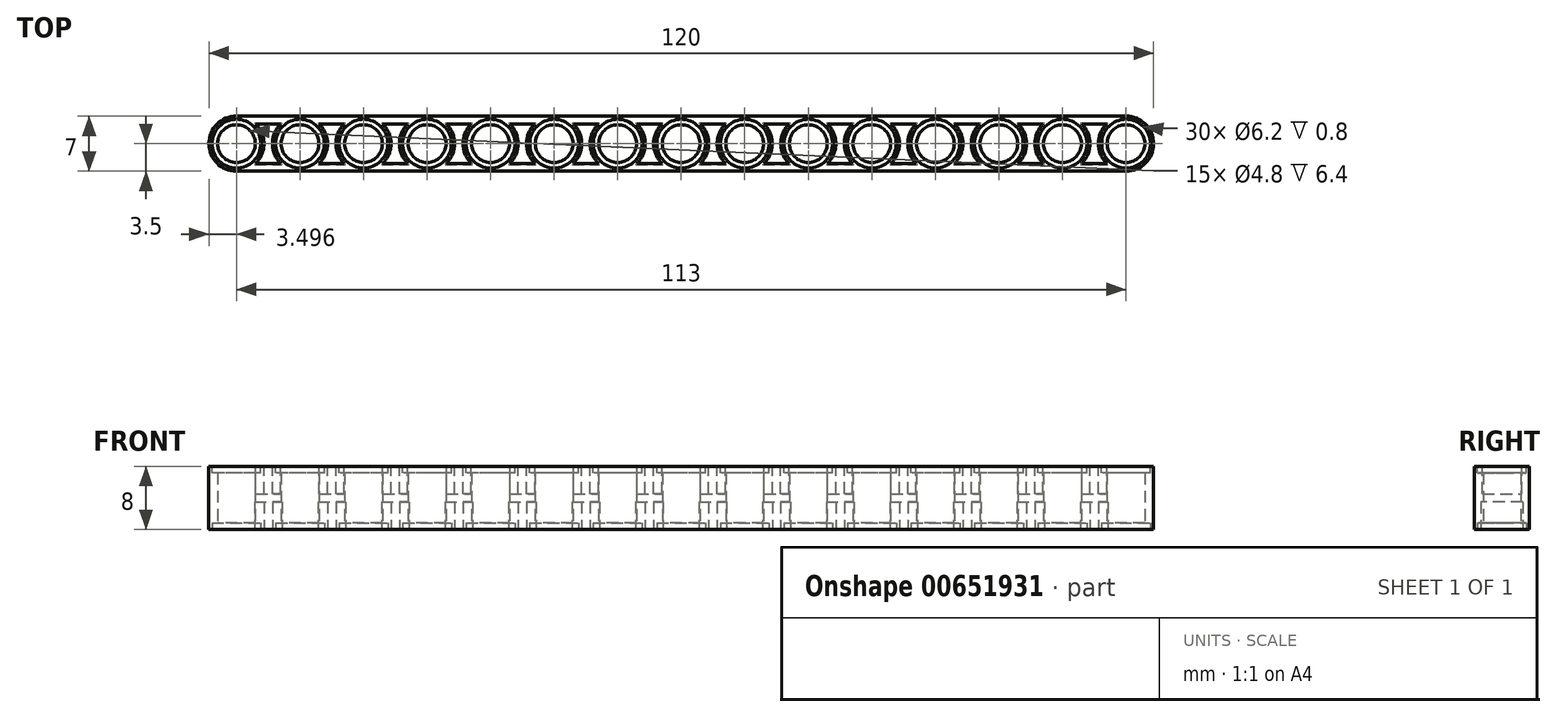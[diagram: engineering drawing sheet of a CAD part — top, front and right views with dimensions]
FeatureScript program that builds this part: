
annotation { "Feature Type Name" : "Feature", "Feature Type Description" : "" }
export const myFeature = defineFeature(function(context is Context, id is Id, definition is map)
    precondition{}
    {
        {
            var Q0;
            Q0=qCreatedBy(makeId("Top.planeOp"),FACE);
            var sketch = newSketch(context, id + "F0", { "sketchPlane" : qUnion([Q0])});
            skLineSegment(sketch, "E0.bottom", {"start": v(-24.08, -14.52) * mm, "end": v(88.92, -14.52) * mm});
            skLineSegment(sketch, "E0.top", {"start": v(-24.08, -21.52) * mm, "end": v(88.92, -21.52) * mm});
            skLineSegment(sketch, "E0.left", {"start": v(-27.58, -18.02) * mm, "end": v(-27.58, -18.02) * mm});
            skLineSegment(sketch, "E0.right", {"start": v(92.42, -18.02) * mm, "end": v(92.42, -18.02) * mm});
            skPoint(sketch, "E1.visualSharp", {"position": v(-27.58, -14.52) * mm});
            skArc(sketch, "E1.filletArc", {"start": v(-24.08, -14.52) * mm, "mid": v(-26.56, -15.55) * mm, "end": v(-27.58, -18.02) * mm});
            skPoint(sketch, "E2.visualSharp", {"position": v(-27.58, -21.52) * mm});
            skArc(sketch, "E2.filletArc", {"start": v(-27.58, -18.02) * mm, "mid": v(-26.56, -20.5) * mm, "end": v(-24.08, -21.52) * mm});
            skPoint(sketch, "E3.visualSharp", {"position": v(92.42, -21.52) * mm});
            skArc(sketch, "E3.filletArc", {"start": v(88.92, -21.52) * mm, "mid": v(91.4, -20.5) * mm, "end": v(92.42, -18.02) * mm});
            skPoint(sketch, "E4.visualSharp", {"position": v(92.42, -14.52) * mm});
            skArc(sketch, "E4.filletArc", {"start": v(92.42, -18.02) * mm, "mid": v(91.4, -15.55) * mm, "end": v(88.92, -14.52) * mm});
            skCircle(sketch, "E5", {"center": v(-24.08, -18.02) * mm, "radius": 2.4 * mm});
            skCircle(sketch, "E6.1.0.0", {"center": v(-16.01, -18.02) * mm, "radius": 2.4 * mm});
            skLineSegment(sketch, "E6.1.0.1", {"start": v(-16.01, -21.52) * mm, "end": v(96.99, -21.52) * mm});
            skCircle(sketch, "E6.2.0.0", {"center": v(-7.94, -18.02) * mm, "radius": 2.4 * mm});
            skLineSegment(sketch, "E6.2.0.1", {"start": v(-7.94, -21.52) * mm, "end": v(105.06, -21.52) * mm});
            skCircle(sketch, "E6.3.0.0", {"center": v(0.13, -18.02) * mm, "radius": 2.4 * mm});
            skLineSegment(sketch, "E6.3.0.1", {"start": v(0.13, -21.52) * mm, "end": v(113.13, -21.52) * mm});
            skCircle(sketch, "E6.4.0.0", {"center": v(8.2, -18.02) * mm, "radius": 2.4 * mm});
            skLineSegment(sketch, "E6.4.0.1", {"start": v(8.2, -21.52) * mm, "end": v(121.2, -21.52) * mm});
            skCircle(sketch, "E6.5.0.0", {"center": v(16.27, -18.02) * mm, "radius": 2.4 * mm});
            skLineSegment(sketch, "E6.5.0.1", {"start": v(16.27, -21.52) * mm, "end": v(129.27, -21.52) * mm});
            skCircle(sketch, "E6.6.0.0", {"center": v(24.34, -18.02) * mm, "radius": 2.4 * mm});
            skCircle(sketch, "E6.7.0.0", {"center": v(32.42, -18.02) * mm, "radius": 2.4 * mm});
            skLineSegment(sketch, "E6.7.0.1", {"start": v(32.42, -21.52) * mm, "end": v(145.42, -21.52) * mm});
            skCircle(sketch, "E6.8.0.0", {"center": v(40.49, -18.02) * mm, "radius": 2.4 * mm});
            skLineSegment(sketch, "E6.8.0.1", {"start": v(40.49, -21.52) * mm, "end": v(153.49, -21.52) * mm});
            skCircle(sketch, "E6.9.0.0", {"center": v(48.56, -18.02) * mm, "radius": 2.4 * mm});
            skLineSegment(sketch, "E6.9.0.1", {"start": v(48.56, -21.52) * mm, "end": v(161.56, -21.52) * mm});
            skCircle(sketch, "E6.10.0.0", {"center": v(56.63, -18.02) * mm, "radius": 2.4 * mm});
            skLineSegment(sketch, "E6.10.0.1", {"start": v(56.63, -21.52) * mm, "end": v(169.63, -21.52) * mm});
            skCircle(sketch, "E6.11.0.0", {"center": v(64.7, -18.02) * mm, "radius": 2.4 * mm});
            skLineSegment(sketch, "E6.11.0.1", {"start": v(64.7, -21.52) * mm, "end": v(177.7, -21.52) * mm});
            skCircle(sketch, "E6.12.0.0", {"center": v(72.77, -18.02) * mm, "radius": 2.4 * mm});
            skLineSegment(sketch, "E6.12.0.1", {"start": v(72.77, -21.52) * mm, "end": v(185.77, -21.52) * mm});
            skCircle(sketch, "E6.13.0.0", {"center": v(80.84, -18.02) * mm, "radius": 2.4 * mm});
            skLineSegment(sketch, "E6.13.0.1", {"start": v(80.84, -21.52) * mm, "end": v(193.84, -21.52) * mm});
            skCircle(sketch, "E6.14.0.0", {"center": v(88.92, -18.02) * mm, "radius": 2.4 * mm});
            skLineSegment(sketch, "E6.direction1", {"start": v(-24.08, -18.02) * mm, "end": v(-16.01, -18.02) * mm, "construction": true});
            skSolve(sketch);
        }
        {
            var Q0;
            Q0=makeQuery(id+"F0.imprint","IMPRINT",FACE,{"disambiguationData":[TD([[makeQuery(id+"F0.imprint","IMPRINT",EDGE,{"derivedFrom":sQuery(id+"F0.wireOp",EDGE,"E0.bottom")}),-1.0]])]});
            extrude(context, id + "F1", {"entities" : qUnion([Q0]), "depth" : 8 * mm, "offsetDistance" : 25 * mm});
        }
        {
            var Q0;
            Q0=makeQuery(id+"F1.opExtrude","CAP_FACE",FACE,{"disambiguationData":[OSD([sQuery(id+"F0.wireOp",EDGE,"E0.bottom"),sQuery(id+"F0.wireOp",EDGE,"E0.top"),sQuery(id+"F0.wireOp",EDGE,"E1.filletArc"),sQuery(id+"F0.wireOp",EDGE,"E2.filletArc"),sQuery(id+"F0.wireOp",EDGE,"E3.filletArc"),sQuery(id+"F0.wireOp",EDGE,"E4.filletArc"),sQuery(id+"F0.wireOp",EDGE,"E5"),sQuery(id+"F0.wireOp",EDGE,"E6.1.0.0"),sQuery(id+"F0.wireOp",EDGE,"E6.1.0.1"),sQuery(id+"F0.wireOp",EDGE,"E6.2.0.0"),sQuery(id+"F0.wireOp",EDGE,"E6.2.0.1"),sQuery(id+"F0.wireOp",EDGE,"E6.3.0.0"),sQuery(id+"F0.wireOp",EDGE,"E6.3.0.1"),sQuery(id+"F0.wireOp",EDGE,"E6.4.0.0"),sQuery(id+"F0.wireOp",EDGE,"E6.4.0.1"),sQuery(id+"F0.wireOp",EDGE,"E6.5.0.0"),sQuery(id+"F0.wireOp",EDGE,"E6.5.0.1"),sQuery(id+"F0.wireOp",EDGE,"E6.6.0.0"),sQuery(id+"F0.wireOp",EDGE,"E6.7.0.0"),sQuery(id+"F0.wireOp",EDGE,"E6.7.0.1"),sQuery(id+"F0.wireOp",EDGE,"E6.8.0.0"),sQuery(id+"F0.wireOp",EDGE,"E6.8.0.1"),sQuery(id+"F0.wireOp",EDGE,"E6.9.0.0"),sQuery(id+"F0.wireOp",EDGE,"E6.9.0.1"),sQuery(id+"F0.wireOp",EDGE,"E6.10.0.0"),sQuery(id+"F0.wireOp",EDGE,"E6.10.0.1"),sQuery(id+"F0.wireOp",EDGE,"E6.11.0.0"),sQuery(id+"F0.wireOp",EDGE,"E6.11.0.1"),sQuery(id+"F0.wireOp",EDGE,"E6.12.0.0"),sQuery(id+"F0.wireOp",EDGE,"E6.12.0.1"),sQuery(id+"F0.wireOp",EDGE,"E6.13.0.0"),sQuery(id+"F0.wireOp",EDGE,"E6.13.0.1"),sQuery(id+"F0.wireOp",EDGE,"E6.14.0.0")])],"isStart":false});
            var sketch = newSketch(context, id + "F2", { "sketchPlane" : qUnion([Q0])});
            skCircle(sketch, "E7", {"center": v(-24.08, -18.02) * mm, "radius": 3.1 * mm});
            skCircle(sketch, "E8.1.0.0", {"center": v(-16.01, -18.02) * mm, "radius": 3.1 * mm});
            skCircle(sketch, "E8.2.0.0", {"center": v(-7.94, -18.02) * mm, "radius": 3.1 * mm});
            skCircle(sketch, "E8.3.0.0", {"center": v(0.13, -18.02) * mm, "radius": 3.1 * mm});
            skCircle(sketch, "E8.4.0.0", {"center": v(8.2, -18.02) * mm, "radius": 3.1 * mm});
            skCircle(sketch, "E8.5.0.0", {"center": v(16.27, -18.02) * mm, "radius": 3.1 * mm});
            skCircle(sketch, "E8.6.0.0", {"center": v(24.34, -18.02) * mm, "radius": 3.1 * mm});
            skCircle(sketch, "E8.7.0.0", {"center": v(32.42, -18.02) * mm, "radius": 3.1 * mm});
            skCircle(sketch, "E8.8.0.0", {"center": v(40.49, -18.02) * mm, "radius": 3.1 * mm});
            skCircle(sketch, "E8.9.0.0", {"center": v(48.56, -18.02) * mm, "radius": 3.1 * mm});
            skCircle(sketch, "E8.10.0.0", {"center": v(56.63, -18.02) * mm, "radius": 3.1 * mm});
            skCircle(sketch, "E8.11.0.0", {"center": v(64.7, -18.02) * mm, "radius": 3.1 * mm});
            skCircle(sketch, "E8.12.0.0", {"center": v(72.77, -18.02) * mm, "radius": 3.1 * mm});
            skCircle(sketch, "E8.13.0.0", {"center": v(80.84, -18.02) * mm, "radius": 3.1 * mm});
            skCircle(sketch, "E8.14.0.0", {"center": v(88.92, -18.02) * mm, "radius": 3.1 * mm});
            skLineSegment(sketch, "E8.direction1", {"start": v(-24.08, -18.02) * mm, "end": v(-16.01, -18.02) * mm, "construction": true});
            skSolve(sketch);
        }
        {
            var Q0;
            Q0=makeQuery(id+"F2.imprint","IMPRINT",FACE,{"disambiguationData":[TD([[makeQuery(id+"F2.imprint","IMPRINT",EDGE,{"derivedFrom":sQuery(id+"F2.wireOp",EDGE,"E8.14.0.0")}),1.0]])]});
            var Q1;
            Q1=makeQuery(id+"F2.imprint","IMPRINT",FACE,{"disambiguationData":[TD([[makeQuery(id+"F2.imprint","IMPRINT",EDGE,{"derivedFrom":sQuery(id+"F2.wireOp",EDGE,"E8.13.0.0")}),1.0]])]});
            var Q2;
            Q2=makeQuery(id+"F2.imprint","IMPRINT",FACE,{"disambiguationData":[TD([[makeQuery(id+"F2.imprint","IMPRINT",EDGE,{"derivedFrom":sQuery(id+"F2.wireOp",EDGE,"E8.12.0.0")}),1.0]])]});
            var Q3;
            Q3=makeQuery(id+"F2.imprint","IMPRINT",FACE,{"disambiguationData":[TD([[makeQuery(id+"F2.imprint","IMPRINT",EDGE,{"derivedFrom":sQuery(id+"F2.wireOp",EDGE,"E8.11.0.0")}),1.0]])]});
            var Q4;
            Q4=makeQuery(id+"F2.imprint","IMPRINT",FACE,{"disambiguationData":[TD([[makeQuery(id+"F2.imprint","IMPRINT",EDGE,{"derivedFrom":sQuery(id+"F2.wireOp",EDGE,"E8.10.0.0")}),1.0]])]});
            var Q5;
            Q5=makeQuery(id+"F2.imprint","IMPRINT",FACE,{"disambiguationData":[TD([[makeQuery(id+"F2.imprint","IMPRINT",EDGE,{"derivedFrom":sQuery(id+"F2.wireOp",EDGE,"E8.9.0.0")}),1.0]])]});
            var Q6;
            Q6=makeQuery(id+"F2.imprint","IMPRINT",FACE,{"disambiguationData":[TD([[makeQuery(id+"F2.imprint","IMPRINT",EDGE,{"derivedFrom":sQuery(id+"F2.wireOp",EDGE,"E8.8.0.0")}),1.0]])]});
            var Q7;
            Q7=makeQuery(id+"F2.imprint","IMPRINT",FACE,{"disambiguationData":[TD([[makeQuery(id+"F2.imprint","IMPRINT",EDGE,{"derivedFrom":sQuery(id+"F2.wireOp",EDGE,"E8.7.0.0")}),1.0]])]});
            var Q8;
            Q8=makeQuery(id+"F2.imprint","IMPRINT",FACE,{"disambiguationData":[TD([[makeQuery(id+"F2.imprint","IMPRINT",EDGE,{"derivedFrom":sQuery(id+"F2.wireOp",EDGE,"E8.6.0.0")}),1.0]])]});
            var Q9;
            Q9=makeQuery(id+"F2.imprint","IMPRINT",FACE,{"disambiguationData":[TD([[makeQuery(id+"F2.imprint","IMPRINT",EDGE,{"derivedFrom":sQuery(id+"F2.wireOp",EDGE,"E8.5.0.0")}),1.0]])]});
            var Q10;
            Q10=makeQuery(id+"F2.imprint","IMPRINT",FACE,{"disambiguationData":[TD([[makeQuery(id+"F2.imprint","IMPRINT",EDGE,{"derivedFrom":sQuery(id+"F2.wireOp",EDGE,"E8.4.0.0")}),1.0]])]});
            var Q11;
            Q11=makeQuery(id+"F2.imprint","IMPRINT",FACE,{"disambiguationData":[TD([[makeQuery(id+"F2.imprint","IMPRINT",EDGE,{"derivedFrom":sQuery(id+"F2.wireOp",EDGE,"E8.3.0.0")}),1.0]])]});
            var Q12;
            Q12=makeQuery(id+"F2.imprint","IMPRINT",FACE,{"disambiguationData":[TD([[makeQuery(id+"F2.imprint","IMPRINT",EDGE,{"derivedFrom":sQuery(id+"F2.wireOp",EDGE,"E8.2.0.0")}),1.0]])]});
            var Q13;
            Q13=makeQuery(id+"F2.imprint","IMPRINT",FACE,{"disambiguationData":[TD([[makeQuery(id+"F2.imprint","IMPRINT",EDGE,{"derivedFrom":sQuery(id+"F2.wireOp",EDGE,"E8.1.0.0")}),1.0]])]});
            var Q14;
            Q14=makeQuery(id+"F2.imprint","IMPRINT",FACE,{"disambiguationData":[TD([[makeQuery(id+"F2.imprint","IMPRINT",EDGE,{"derivedFrom":sQuery(id+"F2.wireOp",EDGE,"E7")}),1.0]])]});
            extrude(context, id + "F3", {"entities" : qUnion([Q0, Q1, Q2, Q3, Q4, Q5, Q6, Q7, Q8, Q9, Q10, Q11, Q12, Q13, Q14]), "operationType" : NewBodyOperationType.REMOVE, "oppositeDirection" : true, "depth" : 0.8 * mm, "offsetDistance" : 25 * mm});
        }
        {
            var Q0;
            Q0=makeQuery(id+"F1.opExtrude","CAP_FACE",FACE,{"disambiguationData":[OSD([sQuery(id+"F0.wireOp",EDGE,"E0.bottom"),sQuery(id+"F0.wireOp",EDGE,"E0.top"),sQuery(id+"F0.wireOp",EDGE,"E1.filletArc"),sQuery(id+"F0.wireOp",EDGE,"E2.filletArc"),sQuery(id+"F0.wireOp",EDGE,"E3.filletArc"),sQuery(id+"F0.wireOp",EDGE,"E4.filletArc"),sQuery(id+"F0.wireOp",EDGE,"E5"),sQuery(id+"F0.wireOp",EDGE,"E6.1.0.0"),sQuery(id+"F0.wireOp",EDGE,"E6.1.0.1"),sQuery(id+"F0.wireOp",EDGE,"E6.2.0.0"),sQuery(id+"F0.wireOp",EDGE,"E6.2.0.1"),sQuery(id+"F0.wireOp",EDGE,"E6.3.0.0"),sQuery(id+"F0.wireOp",EDGE,"E6.3.0.1"),sQuery(id+"F0.wireOp",EDGE,"E6.4.0.0"),sQuery(id+"F0.wireOp",EDGE,"E6.4.0.1"),sQuery(id+"F0.wireOp",EDGE,"E6.5.0.0"),sQuery(id+"F0.wireOp",EDGE,"E6.5.0.1"),sQuery(id+"F0.wireOp",EDGE,"E6.6.0.0"),sQuery(id+"F0.wireOp",EDGE,"E6.7.0.0"),sQuery(id+"F0.wireOp",EDGE,"E6.7.0.1"),sQuery(id+"F0.wireOp",EDGE,"E6.8.0.0"),sQuery(id+"F0.wireOp",EDGE,"E6.8.0.1"),sQuery(id+"F0.wireOp",EDGE,"E6.9.0.0"),sQuery(id+"F0.wireOp",EDGE,"E6.9.0.1"),sQuery(id+"F0.wireOp",EDGE,"E6.10.0.0"),sQuery(id+"F0.wireOp",EDGE,"E6.10.0.1"),sQuery(id+"F0.wireOp",EDGE,"E6.11.0.0"),sQuery(id+"F0.wireOp",EDGE,"E6.11.0.1"),sQuery(id+"F0.wireOp",EDGE,"E6.12.0.0"),sQuery(id+"F0.wireOp",EDGE,"E6.12.0.1"),sQuery(id+"F0.wireOp",EDGE,"E6.13.0.0"),sQuery(id+"F0.wireOp",EDGE,"E6.13.0.1"),sQuery(id+"F0.wireOp",EDGE,"E6.14.0.0")])],"isStart":true});
            var sketch = newSketch(context, id + "F4", { "sketchPlane" : qUnion([Q0])});
            skCircle(sketch, "E9", {"center": v(-24.08, 18.02) * mm, "radius": 3.1 * mm});
            skCircle(sketch, "E10.1.0.0", {"center": v(-16.01, 18.02) * mm, "radius": 3.1 * mm});
            skCircle(sketch, "E10.2.0.0", {"center": v(-7.94, 18.02) * mm, "radius": 3.1 * mm});
            skLineSegment(sketch, "E10.direction1", {"start": v(-24.08, 18.02) * mm, "end": v(-16.01, 18.02) * mm, "construction": true});
            skCircle(sketch, "E11.0.3.0", {"center": v(0.13, 18.02) * mm, "radius": 3.1 * mm});
            skCircle(sketch, "E11.0.4.0", {"center": v(8.2, 18.02) * mm, "radius": 3.1 * mm});
            skCircle(sketch, "E11.0.5.0", {"center": v(16.27, 18.02) * mm, "radius": 3.1 * mm});
            skCircle(sketch, "E11.0.6.0", {"center": v(24.34, 18.02) * mm, "radius": 3.1 * mm});
            skCircle(sketch, "E11.0.7.0", {"center": v(32.42, 18.02) * mm, "radius": 3.1 * mm});
            skCircle(sketch, "E11.0.8.0", {"center": v(40.49, 18.02) * mm, "radius": 3.1 * mm});
            skCircle(sketch, "E11.0.9.0", {"center": v(48.56, 18.02) * mm, "radius": 3.1 * mm});
            skCircle(sketch, "E11.0.10.0", {"center": v(56.63, 18.02) * mm, "radius": 3.1 * mm});
            skCircle(sketch, "E11.0.11.0", {"center": v(64.7, 18.02) * mm, "radius": 3.1 * mm});
            skCircle(sketch, "E11.0.12.0", {"center": v(72.77, 18.02) * mm, "radius": 3.1 * mm});
            skCircle(sketch, "E11.0.13.0", {"center": v(80.84, 18.02) * mm, "radius": 3.1 * mm});
            skCircle(sketch, "E11.0.14.0", {"center": v(88.92, 18.02) * mm, "radius": 3.1 * mm});
            skSolve(sketch);
        }
        {
            var Q0;
            Q0=makeQuery(id+"F4.imprint","IMPRINT",FACE,{"disambiguationData":[TD([[makeQuery(id+"F4.imprint","IMPRINT",EDGE,{"derivedFrom":sQuery(id+"F4.wireOp",EDGE,"E9")}),1.0]])]});
            var Q1;
            Q1=makeQuery(id+"F4.imprint","IMPRINT",FACE,{"disambiguationData":[TD([[makeQuery(id+"F4.imprint","IMPRINT",EDGE,{"derivedFrom":sQuery(id+"F4.wireOp",EDGE,"E10.1.0.0")}),1.0]])]});
            var Q2;
            Q2=makeQuery(id+"F4.imprint","IMPRINT",FACE,{"disambiguationData":[TD([[makeQuery(id+"F4.imprint","IMPRINT",EDGE,{"derivedFrom":sQuery(id+"F4.wireOp",EDGE,"E10.2.0.0")}),1.0]])]});
            var Q3;
            Q3=makeQuery(id+"F4.imprint","IMPRINT",FACE,{"disambiguationData":[TD([[makeQuery(id+"F4.imprint","IMPRINT",EDGE,{"derivedFrom":sQuery(id+"F4.wireOp",EDGE,"E11.0.3.0")}),1.0]])]});
            var Q4;
            Q4=makeQuery(id+"F4.imprint","IMPRINT",FACE,{"disambiguationData":[TD([[makeQuery(id+"F4.imprint","IMPRINT",EDGE,{"derivedFrom":sQuery(id+"F4.wireOp",EDGE,"E11.0.4.0")}),1.0]])]});
            var Q5;
            Q5=makeQuery(id+"F4.imprint","IMPRINT",FACE,{"disambiguationData":[TD([[makeQuery(id+"F4.imprint","IMPRINT",EDGE,{"derivedFrom":sQuery(id+"F4.wireOp",EDGE,"E11.0.5.0")}),1.0]])]});
            var Q6;
            Q6=makeQuery(id+"F4.imprint","IMPRINT",FACE,{"disambiguationData":[TD([[makeQuery(id+"F4.imprint","IMPRINT",EDGE,{"derivedFrom":sQuery(id+"F4.wireOp",EDGE,"E11.0.6.0")}),1.0]])]});
            var Q7;
            Q7=makeQuery(id+"F4.imprint","IMPRINT",FACE,{"disambiguationData":[TD([[makeQuery(id+"F4.imprint","IMPRINT",EDGE,{"derivedFrom":sQuery(id+"F4.wireOp",EDGE,"E11.0.7.0")}),1.0]])]});
            var Q8;
            Q8=makeQuery(id+"F4.imprint","IMPRINT",FACE,{"disambiguationData":[TD([[makeQuery(id+"F4.imprint","IMPRINT",EDGE,{"derivedFrom":sQuery(id+"F4.wireOp",EDGE,"E11.0.8.0")}),1.0]])]});
            var Q9;
            Q9=makeQuery(id+"F4.imprint","IMPRINT",FACE,{"disambiguationData":[TD([[makeQuery(id+"F4.imprint","IMPRINT",EDGE,{"derivedFrom":sQuery(id+"F4.wireOp",EDGE,"E11.0.9.0")}),1.0]])]});
            var Q10;
            Q10=makeQuery(id+"F4.imprint","IMPRINT",FACE,{"disambiguationData":[TD([[makeQuery(id+"F4.imprint","IMPRINT",EDGE,{"derivedFrom":sQuery(id+"F4.wireOp",EDGE,"E11.0.10.0")}),1.0]])]});
            var Q11;
            Q11=makeQuery(id+"F4.imprint","IMPRINT",FACE,{"disambiguationData":[TD([[makeQuery(id+"F4.imprint","IMPRINT",EDGE,{"derivedFrom":sQuery(id+"F4.wireOp",EDGE,"E11.0.11.0")}),1.0]])]});
            var Q12;
            Q12=makeQuery(id+"F4.imprint","IMPRINT",FACE,{"disambiguationData":[TD([[makeQuery(id+"F4.imprint","IMPRINT",EDGE,{"derivedFrom":sQuery(id+"F4.wireOp",EDGE,"E11.0.12.0")}),1.0]])]});
            var Q13;
            Q13=makeQuery(id+"F4.imprint","IMPRINT",FACE,{"disambiguationData":[TD([[makeQuery(id+"F4.imprint","IMPRINT",EDGE,{"derivedFrom":sQuery(id+"F4.wireOp",EDGE,"E11.0.13.0")}),1.0]])]});
            var Q14;
            Q14=makeQuery(id+"F4.imprint","IMPRINT",FACE,{"disambiguationData":[TD([[makeQuery(id+"F4.imprint","IMPRINT",EDGE,{"derivedFrom":sQuery(id+"F4.wireOp",EDGE,"E11.0.14.0")}),1.0]])]});
            extrude(context, id + "F5", {"entities" : qUnion([Q0, Q1, Q2, Q3, Q4, Q5, Q6, Q7, Q8, Q9, Q10, Q11, Q12, Q13, Q14]), "operationType" : NewBodyOperationType.REMOVE, "oppositeDirection" : true, "depth" : 0.8 * mm, "offsetDistance" : 25 * mm});
        }
        {
            var Q0;
            Q0=makeQuery(id+"F1.opExtrude","CAP_FACE",FACE,{"disambiguationData":[OSD([sQuery(id+"F0.wireOp",EDGE,"E0.bottom"),sQuery(id+"F0.wireOp",EDGE,"E0.top"),sQuery(id+"F0.wireOp",EDGE,"E1.filletArc"),sQuery(id+"F0.wireOp",EDGE,"E2.filletArc"),sQuery(id+"F0.wireOp",EDGE,"E3.filletArc"),sQuery(id+"F0.wireOp",EDGE,"E4.filletArc"),sQuery(id+"F0.wireOp",EDGE,"E5"),sQuery(id+"F0.wireOp",EDGE,"E6.1.0.0"),sQuery(id+"F0.wireOp",EDGE,"E6.1.0.1"),sQuery(id+"F0.wireOp",EDGE,"E6.2.0.0"),sQuery(id+"F0.wireOp",EDGE,"E6.2.0.1"),sQuery(id+"F0.wireOp",EDGE,"E6.3.0.0"),sQuery(id+"F0.wireOp",EDGE,"E6.3.0.1"),sQuery(id+"F0.wireOp",EDGE,"E6.4.0.0"),sQuery(id+"F0.wireOp",EDGE,"E6.4.0.1"),sQuery(id+"F0.wireOp",EDGE,"E6.5.0.0"),sQuery(id+"F0.wireOp",EDGE,"E6.5.0.1"),sQuery(id+"F0.wireOp",EDGE,"E6.6.0.0"),sQuery(id+"F0.wireOp",EDGE,"E6.7.0.0"),sQuery(id+"F0.wireOp",EDGE,"E6.7.0.1"),sQuery(id+"F0.wireOp",EDGE,"E6.8.0.0"),sQuery(id+"F0.wireOp",EDGE,"E6.8.0.1"),sQuery(id+"F0.wireOp",EDGE,"E6.9.0.0"),sQuery(id+"F0.wireOp",EDGE,"E6.9.0.1"),sQuery(id+"F0.wireOp",EDGE,"E6.10.0.0"),sQuery(id+"F0.wireOp",EDGE,"E6.10.0.1"),sQuery(id+"F0.wireOp",EDGE,"E6.11.0.0"),sQuery(id+"F0.wireOp",EDGE,"E6.11.0.1"),sQuery(id+"F0.wireOp",EDGE,"E6.12.0.0"),sQuery(id+"F0.wireOp",EDGE,"E6.12.0.1"),sQuery(id+"F0.wireOp",EDGE,"E6.13.0.0"),sQuery(id+"F0.wireOp",EDGE,"E6.13.0.1"),sQuery(id+"F0.wireOp",EDGE,"E6.14.0.0")])],"isStart":true});
            var sketch = newSketch(context, id + "F6", { "sketchPlane" : qUnion([Q0])});
            skCircle(sketch, "E12.0", {"center": v(-24.08, 18.02) * mm, "radius": 3.1 * mm});
            skCircle(sketch, "E13.0", {"center": v(-16.01, 18.02) * mm, "radius": 3.1 * mm});
            skLineSegment(sketch, "E14.0", {"start": v(-24.08, 14.52) * mm, "end": v(88.92, 14.52) * mm});
            skLineSegment(sketch, "E15.0", {"start": v(-24.08, 21.52) * mm, "end": v(88.92, 21.52) * mm});
            skLineSegment(sketch, "E16.0.0", {"start": v(88.92, 21.52) * mm, "end": v(-24.08, 21.52) * mm});
            skArc(sketch, "E16.0.1", {"start": v(-24.08, 21.52) * mm, "mid": v(-27.58, 18.02) * mm, "end": v(-24.08, 14.52) * mm});
            skArc(sketch, "E16.0.3", {"start": v(88.92, 14.52) * mm, "mid": v(92.42, 18.02) * mm, "end": v(88.92, 21.52) * mm});
            skCircle(sketch, "E17", {"center": v(-24.08, 18.02) * mm, "radius": 3.5 * mm});
            skCircle(sketch, "E18.1.0.0", {"center": v(-16.01, 18.02) * mm, "radius": 3.5 * mm});
            skCircle(sketch, "E18.2.0.0", {"center": v(-7.94, 18.02) * mm, "radius": 3.5 * mm});
            skCircle(sketch, "E18.3.0.0", {"center": v(0.13, 18.02) * mm, "radius": 3.5 * mm});
            skCircle(sketch, "E18.4.0.0", {"center": v(8.2, 18.02) * mm, "radius": 3.5 * mm});
            skCircle(sketch, "E18.5.0.0", {"center": v(16.27, 18.02) * mm, "radius": 3.5 * mm});
            skCircle(sketch, "E18.6.0.0", {"center": v(24.34, 18.02) * mm, "radius": 3.5 * mm});
            skCircle(sketch, "E18.7.0.0", {"center": v(32.42, 18.02) * mm, "radius": 3.5 * mm});
            skCircle(sketch, "E18.8.0.0", {"center": v(40.49, 18.02) * mm, "radius": 3.5 * mm});
            skCircle(sketch, "E18.9.0.0", {"center": v(48.56, 18.02) * mm, "radius": 3.5 * mm});
            skCircle(sketch, "E18.10.0.0", {"center": v(56.63, 18.02) * mm, "radius": 3.5 * mm});
            skCircle(sketch, "E18.11.0.0", {"center": v(64.7, 18.02) * mm, "radius": 3.5 * mm});
            skCircle(sketch, "E18.12.0.0", {"center": v(72.77, 18.02) * mm, "radius": 3.5 * mm});
            skCircle(sketch, "E18.13.0.0", {"center": v(80.84, 18.02) * mm, "radius": 3.5 * mm});
            skCircle(sketch, "E18.14.0.0", {"center": v(88.92, 18.02) * mm, "radius": 3.5 * mm});
            skLineSegment(sketch, "E18.direction1", {"start": v(-24.08, 18.02) * mm, "end": v(-16.01, 18.02) * mm, "construction": true});
            skLineSegment(sketch, "E19", {"start": v(-21.8, 15.37) * mm, "end": v(-18.3, 15.37) * mm});
            skLineSegment(sketch, "E20", {"start": v(-21.8, 20.67) * mm, "end": v(-18.3, 20.67) * mm});
            skLineSegment(sketch, "E21.trimOffspring", {"start": v(-13.73, 15.37) * mm, "end": v(-10.23, 15.37) * mm});
            skLineSegment(sketch, "E22.trimOffspring", {"start": v(-13.73, 20.67) * mm, "end": v(-10.23, 20.67) * mm});
            skLineSegment(sketch, "E23.trimOffspring", {"start": v(-5.66, 20.67) * mm, "end": v(-2.15, 20.67) * mm});
            skLineSegment(sketch, "E24.trimOffspring", {"start": v(-5.66, 15.37) * mm, "end": v(-2.15, 15.37) * mm});
            skLineSegment(sketch, "E25.trimOffspring", {"start": v(2.42, 20.67) * mm, "end": v(5.92, 20.67) * mm});
            skLineSegment(sketch, "E26.trimOffspring", {"start": v(2.42, 15.37) * mm, "end": v(5.92, 15.37) * mm});
            skLineSegment(sketch, "E27.trimOffspring", {"start": v(10.49, 20.67) * mm, "end": v(13.99, 20.67) * mm});
            skLineSegment(sketch, "E28.trimOffspring", {"start": v(10.49, 15.37) * mm, "end": v(13.99, 15.37) * mm});
            skLineSegment(sketch, "E29.trimOffspring", {"start": v(18.56, 20.67) * mm, "end": v(22.06, 20.67) * mm});
            skLineSegment(sketch, "E30.trimOffspring", {"start": v(18.56, 15.37) * mm, "end": v(22.06, 15.37) * mm});
            skLineSegment(sketch, "E31.trimOffspring", {"start": v(26.63, 15.37) * mm, "end": v(30.13, 15.37) * mm});
            skLineSegment(sketch, "E32.trimOffspring", {"start": v(26.63, 20.67) * mm, "end": v(30.13, 20.67) * mm});
            skLineSegment(sketch, "E33.trimOffspring", {"start": v(34.7, 20.67) * mm, "end": v(38.2, 20.67) * mm});
            skLineSegment(sketch, "E34.trimOffspring", {"start": v(34.7, 15.37) * mm, "end": v(38.2, 15.37) * mm});
            skLineSegment(sketch, "E35.trimOffspring", {"start": v(42.77, 20.67) * mm, "end": v(46.27, 20.67) * mm});
            skLineSegment(sketch, "E36.trimOffspring", {"start": v(42.77, 15.37) * mm, "end": v(46.27, 15.37) * mm});
            skLineSegment(sketch, "E37.trimOffspring", {"start": v(50.84, 20.67) * mm, "end": v(54.35, 20.67) * mm});
            skLineSegment(sketch, "E38.trimOffspring", {"start": v(58.92, 20.67) * mm, "end": v(62.42, 20.67) * mm});
            skLineSegment(sketch, "E39.trimOffspring", {"start": v(58.92, 15.37) * mm, "end": v(62.42, 15.37) * mm});
            skLineSegment(sketch, "E40.trimOffspring", {"start": v(66.99, 20.67) * mm, "end": v(70.49, 20.67) * mm});
            skLineSegment(sketch, "E41.trimOffspring", {"start": v(66.99, 15.37) * mm, "end": v(70.49, 15.37) * mm});
            skLineSegment(sketch, "E42.trimOffspring", {"start": v(75.06, 15.37) * mm, "end": v(78.56, 15.37) * mm});
            skLineSegment(sketch, "E43.trimOffspring", {"start": v(75.06, 20.67) * mm, "end": v(78.56, 20.67) * mm});
            skLineSegment(sketch, "E44.trimOffspring", {"start": v(83.13, 15.37) * mm, "end": v(86.63, 15.37) * mm});
            skLineSegment(sketch, "E45.trimOffspring", {"start": v(83.13, 20.67) * mm, "end": v(86.63, 20.67) * mm});
            skLineSegment(sketch, "E46", {"start": v(50.84, 15.37) * mm, "end": v(54.35, 15.37) * mm});
            skSolve(sketch);
        }
        {
            var Q0;
            {var subQ0=sQuery(id+"F6.wireOp",EDGE,"E19");Q0=makeQuery(id+"F6.imprint","IMPRINT",FACE,{"disambiguationData":[TD([[makeQuery(id+"F6.imprint","IMPRINT",EDGE,{"derivedFrom":subQ0}),1.0]])]});}
            var Q1;
            {var subQ0=sQuery(id+"F6.wireOp",EDGE,"E21.trimOffspring");Q1=makeQuery(id+"F6.imprint","IMPRINT",FACE,{"disambiguationData":[TD([[makeQuery(id+"F6.imprint","IMPRINT",EDGE,{"derivedFrom":subQ0}),1.0]])]});}
            var Q2;
            {var subQ0=sQuery(id+"F6.wireOp",EDGE,"E23.trimOffspring");Q2=makeQuery(id+"F6.imprint","IMPRINT",FACE,{"disambiguationData":[TD([[makeQuery(id+"F6.imprint","IMPRINT",EDGE,{"derivedFrom":subQ0}),-1.0]])]});}
            var Q3;
            {var subQ0=sQuery(id+"F6.wireOp",EDGE,"E25.trimOffspring");Q3=makeQuery(id+"F6.imprint","IMPRINT",FACE,{"disambiguationData":[TD([[makeQuery(id+"F6.imprint","IMPRINT",EDGE,{"derivedFrom":subQ0}),-1.0]])]});}
            var Q4;
            {var subQ0=sQuery(id+"F6.wireOp",EDGE,"E27.trimOffspring");Q4=makeQuery(id+"F6.imprint","IMPRINT",FACE,{"disambiguationData":[TD([[makeQuery(id+"F6.imprint","IMPRINT",EDGE,{"derivedFrom":subQ0}),-1.0]])]});}
            var Q5;
            {var subQ0=sQuery(id+"F6.wireOp",EDGE,"E29.trimOffspring");Q5=makeQuery(id+"F6.imprint","IMPRINT",FACE,{"disambiguationData":[TD([[makeQuery(id+"F6.imprint","IMPRINT",EDGE,{"derivedFrom":subQ0}),-1.0]])]});}
            var Q6;
            {var subQ0=sQuery(id+"F6.wireOp",EDGE,"E31.trimOffspring");Q6=makeQuery(id+"F6.imprint","IMPRINT",FACE,{"disambiguationData":[TD([[makeQuery(id+"F6.imprint","IMPRINT",EDGE,{"derivedFrom":subQ0}),1.0]])]});}
            var Q7;
            {var subQ0=sQuery(id+"F6.wireOp",EDGE,"E33.trimOffspring");Q7=makeQuery(id+"F6.imprint","IMPRINT",FACE,{"disambiguationData":[TD([[makeQuery(id+"F6.imprint","IMPRINT",EDGE,{"derivedFrom":subQ0}),-1.0]])]});}
            var Q8;
            {var subQ0=sQuery(id+"F6.wireOp",EDGE,"E35.trimOffspring");Q8=makeQuery(id+"F6.imprint","IMPRINT",FACE,{"disambiguationData":[TD([[makeQuery(id+"F6.imprint","IMPRINT",EDGE,{"derivedFrom":subQ0}),-1.0]])]});}
            var Q9;
            {var subQ0=sQuery(id+"F6.wireOp",EDGE,"E37.trimOffspring");Q9=makeQuery(id+"F6.imprint","IMPRINT",FACE,{"disambiguationData":[TD([[makeQuery(id+"F6.imprint","IMPRINT",EDGE,{"derivedFrom":subQ0}),-1.0]])]});}
            var Q10;
            {var subQ0=sQuery(id+"F6.wireOp",EDGE,"E38.trimOffspring");Q10=makeQuery(id+"F6.imprint","IMPRINT",FACE,{"disambiguationData":[TD([[makeQuery(id+"F6.imprint","IMPRINT",EDGE,{"derivedFrom":subQ0}),-1.0]])]});}
            var Q11;
            {var subQ0=sQuery(id+"F6.wireOp",EDGE,"E40.trimOffspring");Q11=makeQuery(id+"F6.imprint","IMPRINT",FACE,{"disambiguationData":[TD([[makeQuery(id+"F6.imprint","IMPRINT",EDGE,{"derivedFrom":subQ0}),-1.0]])]});}
            var Q12;
            {var subQ0=sQuery(id+"F6.wireOp",EDGE,"E42.trimOffspring");Q12=makeQuery(id+"F6.imprint","IMPRINT",FACE,{"disambiguationData":[TD([[makeQuery(id+"F6.imprint","IMPRINT",EDGE,{"derivedFrom":subQ0}),1.0]])]});}
            var Q13;
            {var subQ0=sQuery(id+"F6.wireOp",EDGE,"E44.trimOffspring");Q13=makeQuery(id+"F6.imprint","IMPRINT",FACE,{"disambiguationData":[TD([[makeQuery(id+"F6.imprint","IMPRINT",EDGE,{"derivedFrom":subQ0}),1.0]])]});}
            extrude(context, id + "F7", {"entities" : qUnion([Q0, Q1, Q2, Q3, Q4, Q5, Q6, Q7, Q8, Q9, Q10, Q11, Q12, Q13]), "operationType" : NewBodyOperationType.REMOVE, "oppositeDirection" : true, "depth" : 3.5 * mm, "offsetDistance" : 25 * mm});
        }
        {
            var Q0;
            Q0=makeQuery(id+"F1.opExtrude","CAP_FACE",FACE,{"disambiguationData":[OSD([sQuery(id+"F0.wireOp",EDGE,"E0.bottom"),sQuery(id+"F0.wireOp",EDGE,"E0.top"),sQuery(id+"F0.wireOp",EDGE,"E1.filletArc"),sQuery(id+"F0.wireOp",EDGE,"E2.filletArc"),sQuery(id+"F0.wireOp",EDGE,"E3.filletArc"),sQuery(id+"F0.wireOp",EDGE,"E4.filletArc"),sQuery(id+"F0.wireOp",EDGE,"E5"),sQuery(id+"F0.wireOp",EDGE,"E6.1.0.0"),sQuery(id+"F0.wireOp",EDGE,"E6.1.0.1"),sQuery(id+"F0.wireOp",EDGE,"E6.2.0.0"),sQuery(id+"F0.wireOp",EDGE,"E6.2.0.1"),sQuery(id+"F0.wireOp",EDGE,"E6.3.0.0"),sQuery(id+"F0.wireOp",EDGE,"E6.3.0.1"),sQuery(id+"F0.wireOp",EDGE,"E6.4.0.0"),sQuery(id+"F0.wireOp",EDGE,"E6.4.0.1"),sQuery(id+"F0.wireOp",EDGE,"E6.5.0.0"),sQuery(id+"F0.wireOp",EDGE,"E6.5.0.1"),sQuery(id+"F0.wireOp",EDGE,"E6.6.0.0"),sQuery(id+"F0.wireOp",EDGE,"E6.7.0.0"),sQuery(id+"F0.wireOp",EDGE,"E6.7.0.1"),sQuery(id+"F0.wireOp",EDGE,"E6.8.0.0"),sQuery(id+"F0.wireOp",EDGE,"E6.8.0.1"),sQuery(id+"F0.wireOp",EDGE,"E6.9.0.0"),sQuery(id+"F0.wireOp",EDGE,"E6.9.0.1"),sQuery(id+"F0.wireOp",EDGE,"E6.10.0.0"),sQuery(id+"F0.wireOp",EDGE,"E6.10.0.1"),sQuery(id+"F0.wireOp",EDGE,"E6.11.0.0"),sQuery(id+"F0.wireOp",EDGE,"E6.11.0.1"),sQuery(id+"F0.wireOp",EDGE,"E6.12.0.0"),sQuery(id+"F0.wireOp",EDGE,"E6.12.0.1"),sQuery(id+"F0.wireOp",EDGE,"E6.13.0.0"),sQuery(id+"F0.wireOp",EDGE,"E6.13.0.1"),sQuery(id+"F0.wireOp",EDGE,"E6.14.0.0")])],"isStart":false});
            var sketch = newSketch(context, id + "F8", { "sketchPlane" : qUnion([Q0])});
            skLineSegment(sketch, "E47.0", {"start": v(-22.25, -20.52) * mm, "end": v(-17.85, -20.52) * mm});
            skLineSegment(sketch, "E48.0", {"start": v(-22.25, -15.52) * mm, "end": v(-17.85, -15.52) * mm});
            skLineSegment(sketch, "E49.0.0", {"start": v(-24.08, -21.52) * mm, "end": v(88.92, -21.52) * mm});
            skArc(sketch, "E49.0.1", {"start": v(88.92, -21.52) * mm, "mid": v(92.42, -18.02) * mm, "end": v(88.92, -14.52) * mm});
            skLineSegment(sketch, "E49.0.2", {"start": v(88.92, -14.52) * mm, "end": v(-24.08, -14.52) * mm});
            skArc(sketch, "E49.0.3", {"start": v(-24.08, -14.52) * mm, "mid": v(-27.58, -18.02) * mm, "end": v(-24.08, -21.52) * mm});
            skCircle(sketch, "E50.0", {"center": v(-24.08, -18.02) * mm, "radius": 3.1 * mm});
            skCircle(sketch, "E51.0", {"center": v(-16.01, -18.02) * mm, "radius": 3.1 * mm});
            skCircle(sketch, "E52.0", {"center": v(-7.94, -18.02) * mm, "radius": 3.1 * mm});
            skCircle(sketch, "E53.0", {"center": v(8.2, -18.02) * mm, "radius": 3.1 * mm});
            skCircle(sketch, "E54.0", {"center": v(16.27, -18.02) * mm, "radius": 3.1 * mm});
            skCircle(sketch, "E55.0", {"center": v(24.34, -18.02) * mm, "radius": 3.1 * mm});
            skCircle(sketch, "E56.0", {"center": v(32.42, -18.02) * mm, "radius": 3.1 * mm});
            skCircle(sketch, "E57.0", {"center": v(40.49, -18.02) * mm, "radius": 3.1 * mm});
            skCircle(sketch, "E58.0", {"center": v(48.56, -18.02) * mm, "radius": 3.1 * mm});
            skCircle(sketch, "E59.0", {"center": v(56.63, -18.02) * mm, "radius": 3.1 * mm});
            skCircle(sketch, "E60.0", {"center": v(64.7, -18.02) * mm, "radius": 3.1 * mm});
            skCircle(sketch, "E61.0", {"center": v(72.77, -18.02) * mm, "radius": 3.1 * mm});
            skCircle(sketch, "E62.0", {"center": v(80.84, -18.02) * mm, "radius": 3.1 * mm});
            skCircle(sketch, "E63.0", {"center": v(88.92, -18.02) * mm, "radius": 3.1 * mm});
            skLineSegment(sketch, "E64.trimOffspring", {"start": v(-14.18, -20.52) * mm, "end": v(-9.77, -20.52) * mm});
            skLineSegment(sketch, "E65.trimOffspring", {"start": v(-14.18, -15.52) * mm, "end": v(-9.77, -15.52) * mm});
            skLineSegment(sketch, "E66.trimOffspring", {"start": v(-6.1, -15.52) * mm, "end": v(-1.7, -15.52) * mm});
            skLineSegment(sketch, "E67.trimOffspring", {"start": v(-6.1, -20.52) * mm, "end": v(-1.7, -20.52) * mm});
            skCircle(sketch, "E68.0", {"center": v(0.13, -18.02) * mm, "radius": 3.1 * mm});
            skLineSegment(sketch, "E69.trimOffspring", {"start": v(1.96, -15.52) * mm, "end": v(6.37, -15.52) * mm});
            skLineSegment(sketch, "E70.trimOffspring", {"start": v(1.96, -20.52) * mm, "end": v(6.37, -20.52) * mm});
            skLineSegment(sketch, "E71.trimOffspring", {"start": v(10.04, -20.52) * mm, "end": v(14.44, -20.52) * mm});
            skLineSegment(sketch, "E72.trimOffspring", {"start": v(10.04, -15.52) * mm, "end": v(14.44, -15.52) * mm});
            skLineSegment(sketch, "E73.trimOffspring", {"start": v(18.1, -15.52) * mm, "end": v(22.51, -15.52) * mm});
            skLineSegment(sketch, "E74.trimOffspring", {"start": v(18.1, -20.52) * mm, "end": v(22.51, -20.52) * mm});
            skLineSegment(sketch, "E75.trimOffspring", {"start": v(26.18, -15.52) * mm, "end": v(30.58, -15.52) * mm});
            skLineSegment(sketch, "E76.trimOffspring", {"start": v(26.18, -20.52) * mm, "end": v(30.58, -20.52) * mm});
            skLineSegment(sketch, "E77.trimOffspring", {"start": v(34.25, -20.52) * mm, "end": v(38.65, -20.52) * mm});
            skLineSegment(sketch, "E78.trimOffspring", {"start": v(34.25, -15.52) * mm, "end": v(38.65, -15.52) * mm});
            skLineSegment(sketch, "E79.trimOffspring", {"start": v(42.32, -20.52) * mm, "end": v(46.73, -20.52) * mm});
            skLineSegment(sketch, "E80.trimOffspring", {"start": v(42.32, -15.52) * mm, "end": v(46.73, -15.52) * mm});
            skLineSegment(sketch, "E81.trimOffspring", {"start": v(50.4, -20.52) * mm, "end": v(54.8, -20.52) * mm});
            skLineSegment(sketch, "E82.trimOffspring", {"start": v(50.4, -15.52) * mm, "end": v(54.8, -15.52) * mm});
            skLineSegment(sketch, "E83.trimOffspring", {"start": v(58.46, -20.52) * mm, "end": v(62.87, -20.52) * mm});
            skLineSegment(sketch, "E84.trimOffspring", {"start": v(58.46, -15.52) * mm, "end": v(62.87, -15.52) * mm});
            skLineSegment(sketch, "E85.trimOffspring", {"start": v(66.54, -15.52) * mm, "end": v(70.94, -15.52) * mm});
            skLineSegment(sketch, "E86.trimOffspring", {"start": v(66.54, -20.52) * mm, "end": v(70.94, -20.52) * mm});
            skLineSegment(sketch, "E87.trimOffspring", {"start": v(74.6, -20.52) * mm, "end": v(79.01, -20.52) * mm});
            skLineSegment(sketch, "E88.trimOffspring", {"start": v(74.6, -15.52) * mm, "end": v(79.01, -15.52) * mm});
            skLineSegment(sketch, "E89.trimOffspring", {"start": v(82.68, -15.52) * mm, "end": v(87.08, -15.52) * mm});
            skLineSegment(sketch, "E90.trimOffspring", {"start": v(82.68, -20.52) * mm, "end": v(87.08, -20.52) * mm});
            skCircle(sketch, "E91", {"center": v(-24.08, -18.02) * mm, "radius": 3.5 * mm});
            skCircle(sketch, "E92.1.0.0", {"center": v(-16.01, -18.02) * mm, "radius": 3.5 * mm});
            skCircle(sketch, "E92.2.0.0", {"center": v(-7.94, -18.02) * mm, "radius": 3.5 * mm});
            skCircle(sketch, "E92.3.0.0", {"center": v(0.13, -18.02) * mm, "radius": 3.5 * mm});
            skCircle(sketch, "E92.4.0.0", {"center": v(8.2, -18.02) * mm, "radius": 3.5 * mm});
            skCircle(sketch, "E92.5.0.0", {"center": v(16.27, -18.02) * mm, "radius": 3.5 * mm});
            skCircle(sketch, "E92.6.0.0", {"center": v(24.34, -18.02) * mm, "radius": 3.5 * mm});
            skCircle(sketch, "E92.7.0.0", {"center": v(32.42, -18.02) * mm, "radius": 3.5 * mm});
            skCircle(sketch, "E92.8.0.0", {"center": v(40.49, -18.02) * mm, "radius": 3.5 * mm});
            skCircle(sketch, "E92.9.0.0", {"center": v(48.56, -18.02) * mm, "radius": 3.5 * mm});
            skCircle(sketch, "E92.10.0.0", {"center": v(56.63, -18.02) * mm, "radius": 3.5 * mm});
            skCircle(sketch, "E92.11.0.0", {"center": v(64.7, -18.02) * mm, "radius": 3.5 * mm});
            skCircle(sketch, "E92.12.0.0", {"center": v(72.77, -18.02) * mm, "radius": 3.5 * mm});
            skCircle(sketch, "E92.13.0.0", {"center": v(80.84, -18.02) * mm, "radius": 3.5 * mm});
            skCircle(sketch, "E92.14.0.0", {"center": v(88.92, -18.02) * mm, "radius": 3.5 * mm});
            skLineSegment(sketch, "E92.direction1", {"start": v(-24.08, -18.02) * mm, "end": v(-16.01, -18.02) * mm, "construction": true});
            skSolve(sketch);
        }
        {
            var Q0;
            {var subQ0=sQuery(id+"F8.wireOp",EDGE,"E91");var subQ1=sQuery(id+"F8.wireOp",EDGE,"E47.0");var subQ2=makeQuery(id+"F8.imprint","INTERSECT",VERTEX,{"derivedFrom":[subQ1,subQ0]});Q0=makeQuery(id+"F8.imprint","IMPRINT",FACE,{"disambiguationData":[TD([[makeQuery(id+"F8.imprint","IMPRINT",EDGE,{"disambiguationData":[TD([[subQ2,-1.0]])],"derivedFrom":subQ1}),1.0]])]});}
            var Q1;
            {var subQ0=sQuery(id+"F8.wireOp",EDGE,"E92.1.0.0");var subQ1=sQuery(id+"F8.wireOp",EDGE,"E64.trimOffspring");var subQ2=makeQuery(id+"F8.imprint","INTERSECT",VERTEX,{"derivedFrom":[subQ1,subQ0]});Q1=makeQuery(id+"F8.imprint","IMPRINT",FACE,{"disambiguationData":[TD([[makeQuery(id+"F8.imprint","IMPRINT",EDGE,{"disambiguationData":[TD([[subQ2,-1.0]])],"derivedFrom":subQ1}),1.0]])]});}
            var Q2;
            {var subQ0=sQuery(id+"F8.wireOp",EDGE,"E92.2.0.0");var subQ1=sQuery(id+"F8.wireOp",EDGE,"E66.trimOffspring");var subQ2=makeQuery(id+"F8.imprint","INTERSECT",VERTEX,{"derivedFrom":[subQ1,subQ0]});Q2=makeQuery(id+"F8.imprint","IMPRINT",FACE,{"disambiguationData":[TD([[makeQuery(id+"F8.imprint","IMPRINT",EDGE,{"disambiguationData":[TD([[subQ2,-1.0]])],"derivedFrom":subQ1}),-1.0]])]});}
            var Q3;
            {var subQ0=sQuery(id+"F8.wireOp",EDGE,"E92.3.0.0");var subQ1=sQuery(id+"F8.wireOp",EDGE,"E69.trimOffspring");var subQ2=makeQuery(id+"F8.imprint","INTERSECT",VERTEX,{"derivedFrom":[subQ1,subQ0]});Q3=makeQuery(id+"F8.imprint","IMPRINT",FACE,{"disambiguationData":[TD([[makeQuery(id+"F8.imprint","IMPRINT",EDGE,{"disambiguationData":[TD([[subQ2,-1.0]])],"derivedFrom":subQ1}),-1.0]])]});}
            var Q4;
            {var subQ0=sQuery(id+"F8.wireOp",EDGE,"E92.4.0.0");var subQ1=sQuery(id+"F8.wireOp",EDGE,"E71.trimOffspring");var subQ2=makeQuery(id+"F8.imprint","INTERSECT",VERTEX,{"derivedFrom":[subQ1,subQ0]});Q4=makeQuery(id+"F8.imprint","IMPRINT",FACE,{"disambiguationData":[TD([[makeQuery(id+"F8.imprint","IMPRINT",EDGE,{"disambiguationData":[TD([[subQ2,-1.0]])],"derivedFrom":subQ1}),1.0]])]});}
            var Q5;
            {var subQ0=sQuery(id+"F8.wireOp",EDGE,"E92.5.0.0");var subQ1=sQuery(id+"F8.wireOp",EDGE,"E73.trimOffspring");var subQ2=makeQuery(id+"F8.imprint","INTERSECT",VERTEX,{"derivedFrom":[subQ1,subQ0]});Q5=makeQuery(id+"F8.imprint","IMPRINT",FACE,{"disambiguationData":[TD([[makeQuery(id+"F8.imprint","IMPRINT",EDGE,{"disambiguationData":[TD([[subQ2,-1.0]])],"derivedFrom":subQ1}),-1.0]])]});}
            var Q6;
            {var subQ0=sQuery(id+"F8.wireOp",EDGE,"E92.6.0.0");var subQ1=sQuery(id+"F8.wireOp",EDGE,"E75.trimOffspring");var subQ2=makeQuery(id+"F8.imprint","INTERSECT",VERTEX,{"derivedFrom":[subQ1,subQ0]});Q6=makeQuery(id+"F8.imprint","IMPRINT",FACE,{"disambiguationData":[TD([[makeQuery(id+"F8.imprint","IMPRINT",EDGE,{"disambiguationData":[TD([[subQ2,-1.0]])],"derivedFrom":subQ1}),-1.0]])]});}
            var Q7;
            {var subQ0=sQuery(id+"F8.wireOp",EDGE,"E92.7.0.0");var subQ1=sQuery(id+"F8.wireOp",EDGE,"E77.trimOffspring");var subQ2=makeQuery(id+"F8.imprint","INTERSECT",VERTEX,{"derivedFrom":[subQ1,subQ0]});Q7=makeQuery(id+"F8.imprint","IMPRINT",FACE,{"disambiguationData":[TD([[makeQuery(id+"F8.imprint","IMPRINT",EDGE,{"disambiguationData":[TD([[subQ2,-1.0]])],"derivedFrom":subQ1}),1.0]])]});}
            var Q8;
            {var subQ0=sQuery(id+"F8.wireOp",EDGE,"E92.8.0.0");var subQ1=sQuery(id+"F8.wireOp",EDGE,"E79.trimOffspring");var subQ2=makeQuery(id+"F8.imprint","INTERSECT",VERTEX,{"derivedFrom":[subQ1,subQ0]});Q8=makeQuery(id+"F8.imprint","IMPRINT",FACE,{"disambiguationData":[TD([[makeQuery(id+"F8.imprint","IMPRINT",EDGE,{"disambiguationData":[TD([[subQ2,-1.0]])],"derivedFrom":subQ1}),1.0]])]});}
            var Q9;
            {var subQ0=sQuery(id+"F8.wireOp",EDGE,"E92.9.0.0");var subQ1=sQuery(id+"F8.wireOp",EDGE,"E81.trimOffspring");var subQ2=makeQuery(id+"F8.imprint","INTERSECT",VERTEX,{"derivedFrom":[subQ1,subQ0]});Q9=makeQuery(id+"F8.imprint","IMPRINT",FACE,{"disambiguationData":[TD([[makeQuery(id+"F8.imprint","IMPRINT",EDGE,{"disambiguationData":[TD([[subQ2,-1.0]])],"derivedFrom":subQ1}),1.0]])]});}
            var Q10;
            {var subQ0=sQuery(id+"F8.wireOp",EDGE,"E92.10.0.0");var subQ1=sQuery(id+"F8.wireOp",EDGE,"E83.trimOffspring");var subQ2=makeQuery(id+"F8.imprint","INTERSECT",VERTEX,{"derivedFrom":[subQ1,subQ0]});Q10=makeQuery(id+"F8.imprint","IMPRINT",FACE,{"disambiguationData":[TD([[makeQuery(id+"F8.imprint","IMPRINT",EDGE,{"disambiguationData":[TD([[subQ2,-1.0]])],"derivedFrom":subQ1}),1.0]])]});}
            var Q11;
            {var subQ0=sQuery(id+"F8.wireOp",EDGE,"E92.11.0.0");var subQ1=sQuery(id+"F8.wireOp",EDGE,"E85.trimOffspring");var subQ2=makeQuery(id+"F8.imprint","INTERSECT",VERTEX,{"derivedFrom":[subQ1,subQ0]});Q11=makeQuery(id+"F8.imprint","IMPRINT",FACE,{"disambiguationData":[TD([[makeQuery(id+"F8.imprint","IMPRINT",EDGE,{"disambiguationData":[TD([[subQ2,-1.0]])],"derivedFrom":subQ1}),-1.0]])]});}
            var Q12;
            {var subQ0=sQuery(id+"F8.wireOp",EDGE,"E92.12.0.0");var subQ1=sQuery(id+"F8.wireOp",EDGE,"E87.trimOffspring");var subQ2=makeQuery(id+"F8.imprint","INTERSECT",VERTEX,{"derivedFrom":[subQ1,subQ0]});Q12=makeQuery(id+"F8.imprint","IMPRINT",FACE,{"disambiguationData":[TD([[makeQuery(id+"F8.imprint","IMPRINT",EDGE,{"disambiguationData":[TD([[subQ2,-1.0]])],"derivedFrom":subQ1}),1.0]])]});}
            var Q13;
            {var subQ0=sQuery(id+"F8.wireOp",EDGE,"E92.13.0.0");var subQ1=sQuery(id+"F8.wireOp",EDGE,"E89.trimOffspring");var subQ2=makeQuery(id+"F8.imprint","INTERSECT",VERTEX,{"derivedFrom":[subQ1,subQ0]});Q13=makeQuery(id+"F8.imprint","IMPRINT",FACE,{"disambiguationData":[TD([[makeQuery(id+"F8.imprint","IMPRINT",EDGE,{"disambiguationData":[TD([[subQ2,-1.0]])],"derivedFrom":subQ1}),-1.0]])]});}
            extrude(context, id + "F9", {"entities" : qUnion([Q0, Q1, Q2, Q3, Q4, Q5, Q6, Q7, Q8, Q9, Q10, Q11, Q12, Q13]), "operationType" : NewBodyOperationType.REMOVE, "oppositeDirection" : true, "depth" : 3.5 * mm, "offsetDistance" : 25 * mm});
        }
    });
